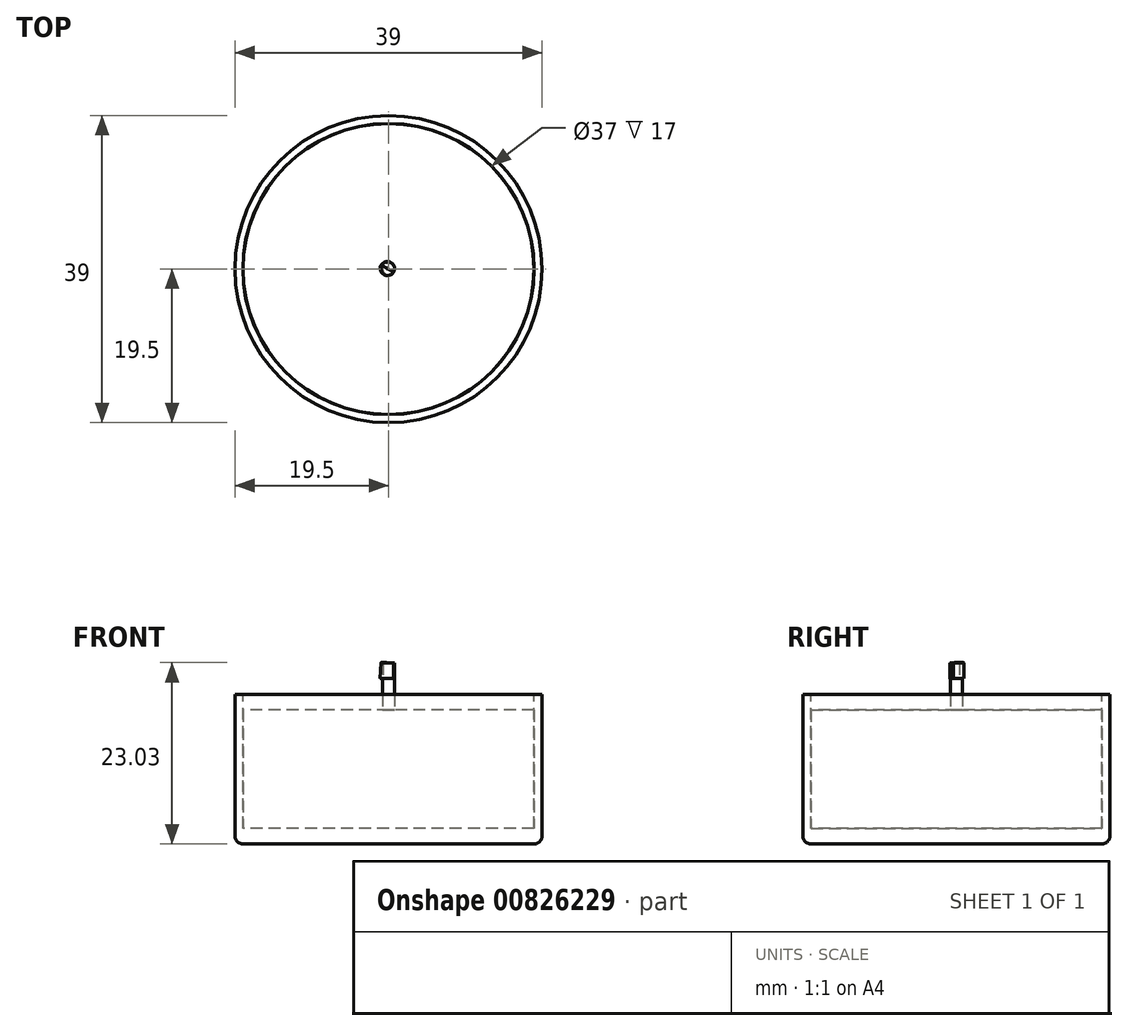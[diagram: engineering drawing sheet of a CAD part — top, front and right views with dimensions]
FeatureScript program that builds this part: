
annotation { "Feature Type Name" : "Feature", "Feature Type Description" : "" }
export const myFeature = defineFeature(function(context is Context, id is Id, definition is map)
    precondition{}
    {
        {
            var Q0;
            Q0=qCreatedBy(makeId("Top.planeOp"),FACE);
            var sketch = newSketch(context, id + "F0", { "sketchPlane" : qUnion([Q0])});
            skCircle(sketch, "E0", {"center": v(0, 0) * mm, "radius": 19.5 * mm});
            skSolve(sketch);
        }
        {
            var Q0;
            Q0=makeQuery(id+"F0.imprint","IMPRINT",FACE,{"disambiguationData":[TD([[makeQuery(id+"F0.imprint","IMPRINT",EDGE,{"derivedFrom":sQuery(id+"F0.wireOp",EDGE,"E0")}),1.0]])]});
            extrude(context, id + "F1", {"entities" : qUnion([Q0]), "depth" : 19 * mm, "offsetDistance" : 25 * mm});
        }
        {
            var Q0;
            Q0=makeQuery(id+"F1.opExtrude","CAP_EDGE",EDGE,{"disambiguationData":[OSD([sQuery(id+"F0.wireOp",EDGE,"E0")])],"isStart":true});
            fillet(context, id + "F2", {"entities" : qUnion([Q0]), "radius" : 1 * mm, "tangentPropagation" : true, "allowEdgeOverflow" : false});
        }
        {
            var Q0;
            Q0=makeQuery(id+"F1.opExtrude","CAP_FACE",FACE,{"disambiguationData":[OSD([sQuery(id+"F0.wireOp",EDGE,"E0")])],"isStart":false});
            var sketch = newSketch(context, id + "F3", { "sketchPlane" : qUnion([Q0])});
            skCircle(sketch, "E1", {"center": v(0, 0) * mm, "radius": 18.5 * mm});
            skSolve(sketch);
        }
        {
            var Q0;
            Q0=makeQuery(id+"F3.imprint","IMPRINT",FACE,{"disambiguationData":[TD([[makeQuery(id+"F3.imprint","IMPRINT",EDGE,{"derivedFrom":sQuery(id+"F3.wireOp",EDGE,"E1")}),1.0]])]});
            extrude(context, id + "F4", {"entities" : qUnion([Q0]), "operationType" : NewBodyOperationType.REMOVE, "oppositeDirection" : true, "depth" : 17 * mm, "offsetDistance" : 25 * mm});
        }
        {
            var Q0;
            Q0=makeQuery(id+"F4.boolean.opBoolean","COPY",FACE,{"derivedFrom":makeQuery(id+"F4.opExtrude","CAP_FACE",FACE,{"disambiguationData":[OSD([sQuery(id+"F3.wireOp",EDGE,"E1")])],"isStart":false})});
            var sketch = newSketch(context, id + "F5", { "sketchPlane" : qUnion([Q0])});
            skCircle(sketch, "E2", {"center": v(0, 0) * mm, "radius": 18.48 * mm});
            skSolve(sketch);
        }
        {
            var Q0;
            Q0=makeQuery(id+"F5.imprint","IMPRINT",FACE,{"disambiguationData":[TD([[makeQuery(id+"F5.imprint","IMPRINT",EDGE,{"derivedFrom":sQuery(id+"F5.wireOp",EDGE,"E2")}),1.0]])]});
            extrude(context, id + "F6", {"entities" : qUnion([Q0]), "depth" : 15 * mm, "offsetDistance" : 25 * mm});
        }
        {
            var Q0;
            Q0=makeQuery(id+"F6.opExtrude","CAP_FACE",FACE,{"disambiguationData":[OSD([sQuery(id+"F5.wireOp",EDGE,"E2")])],"isStart":false});
            var sketch = newSketch(context, id + "F7", { "sketchPlane" : qUnion([Q0])});
            skCircle(sketch, "E3", {"center": v(0, 0) * mm, "radius": 0.75 * mm});
            skSolve(sketch);
        }
        {
            var Q0;
            Q0=makeQuery(id+"F7.imprint","IMPRINT",FACE,{"disambiguationData":[TD([[makeQuery(id+"F7.imprint","IMPRINT",EDGE,{"derivedFrom":sQuery(id+"F7.wireOp",EDGE,"E3")}),1.0]])]});
            extrude(context, id + "F8", {"entities" : qUnion([Q0]), "operationType" : NewBodyOperationType.ADD, "depth" : 4 * mm, "offsetDistance" : 25 * mm});
        }
        {
            var Q0;
            Q0=makeQuery(id+"F8.opExtrude","CAP_FACE",FACE,{"disambiguationData":[OSD([sQuery(id+"F7.wireOp",EDGE,"E3")])],"isStart":false});
            var sketch = newSketch(context, id + "F9", { "sketchPlane" : qUnion([Q0])});
            skArc(sketch, "E4", {"start": v(-0.66, 0.35) * mm, "mid": v(-0.35, -0.66) * mm, "end": v(0.66, -0.35) * mm});
            skLineSegment(sketch, "E5", {"start": v(0, 0) * mm, "end": v(-0.66, 0.35) * mm});
            skLineSegment(sketch, "E6", {"start": v(-0.66, 0.35) * mm, "end": v(0, 0) * mm});
            skLineSegment(sketch, "E7", {"start": v(0, 0) * mm, "end": v(0.66, -0.35) * mm});
            skSolve(sketch);
        }
        {
            var Q0;
            Q0=makeQuery(id+"F9.imprint","IMPRINT",FACE,{"disambiguationData":[TD([[makeQuery(id+"F9.imprint","IMPRINT",EDGE,{"derivedFrom":sQuery(id+"F9.wireOp",EDGE,"E4")}),1.0]])]});
            var sketch = newSketch(context, id + "F10", { "sketchPlane" : qUnion([Q0])});
            skSolve(sketch);
        }
        {
            var Q0;
            Q0=makeQuery(id+"F10.imprint","IMPRINT",FACE,{"disambiguationData":[TD([[makeQuery(id+"F10.imprint","IMPRINT",EDGE,{"derivedFrom":makeQuery(id+"F9.imprint","IMPRINT",EDGE,{"derivedFrom":sQuery(id+"F9.wireOp",EDGE,"E4")})}),1.0]])]});
            extrude(context, id + "F11", {"entities" : qUnion([Q0]), "operationType" : NewBodyOperationType.ADD, "depth" : 2 * mm, "offsetDistance" : 25 * mm});
        }
        {
            var Q0;
            Q0=makeQuery(id+"F11.opExtrude","SWEPT_FACE",FACE,{"disambiguationData":[OSD([sQuery(id+"F9.wireOp",EDGE,"E6"),sQuery(id+"F9.wireOp",EDGE,"E7")])]});
            var sketch = newSketch(context, id + "F12", { "sketchPlane" : qUnion([Q0])});
            skPoint(sketch, "E8.2.internal.snap0", {"position": v(0, 21) * mm});
            skPoint(sketch, "E8.5.internal.snap0", {"position": v(0, 23) * mm});
            skFitSpline(sketch, "E8", {"points": [v(0.2, 21) * mm, v(0, 21) * mm, v(0, 19.37) * mm, v(4.3, 20.73) * mm, v(2.15, 26.22) * mm, v(0, 29.23) * mm], "startDerivative": vector(-2.63, 1.07) * mm, "endDerivative": vector(-6.72, 5.23) * mm});
            skLineSegment(sketch, "E9", {"start": v(0, 29.23) * mm, "end": v(0.2, 19.23) * mm});
            skSolve(sketch);
        }
        {
            var Q0;
            {var subQ4=sQuery(id+"F9.wireOp",EDGE,"E6");var subQ10=makeQuery(id+"F11.opExtrude","SWEPT_EDGE",EDGE,{"disambiguationData":[OSD([sQuery(id+"F9.wireOp",EDGE,"E4"),subQ4])]});Q0=makeQuery(id+"F12.imprint","IMPRINT",FACE,{"disambiguationData":[TD([[makeQuery(id+"F12.imprint","IMPRINT",EDGE,{"derivedFrom":subQ10}),1.0]])]});}
            var Q1;
            Q1=sQuery(id+"F12.wireOp",EDGE,"E9");
            revolve(context, id + "F13", {"surfaceOperationType" : NewSurfaceOperationType.NEW, "entities" : qUnion([Q0]), "axis" : qUnion([Q1]), "revolveType" : RevolveType.FULL});
        }
    });
